# Revit family: janela de canto
name_source: partatom
category: Windows
revit_build: Autodesk Revit Architecture 2012 (Build: 20110309_2315(x64)
units: mm (PartAtom-declared; Revit-internal decimal feet)

## types (2) — shared parameters
Default Sill Height = 900 mm  [stored 2.95276 ft]
Frame Material = <By Category>
Frame Thickness = 40 mm  [stored 0.131234 ft]
Frame Width = 40 mm  [stored 0.131234 ft]
Glass Position = 15 mm  [stored 0.0492126 ft]
Inset = 40 mm  [stored 0.131234 ft]
Wall Angle to host the corner window = 90.00°
Wall Closure = By host
vidro = Glass

## per-type parameters (varying)
| type | Height | Width | Width of Window B |
| Corner_Window_2366 | 1200 mm | 1000 mm  [stored 3.28084 ft] | 1000 mm  [stored 3.28084 ft] |
| J/01 | 2800 mm | 1500 mm | 1500 mm |

note: [stored X ft] marks values corroborated as IEEE doubles in the binary element streams (Revit-internal decimal feet)

## geometry (parser evidence)
native form markers: Sweep x12
no freeform markers — native parametric forms only
